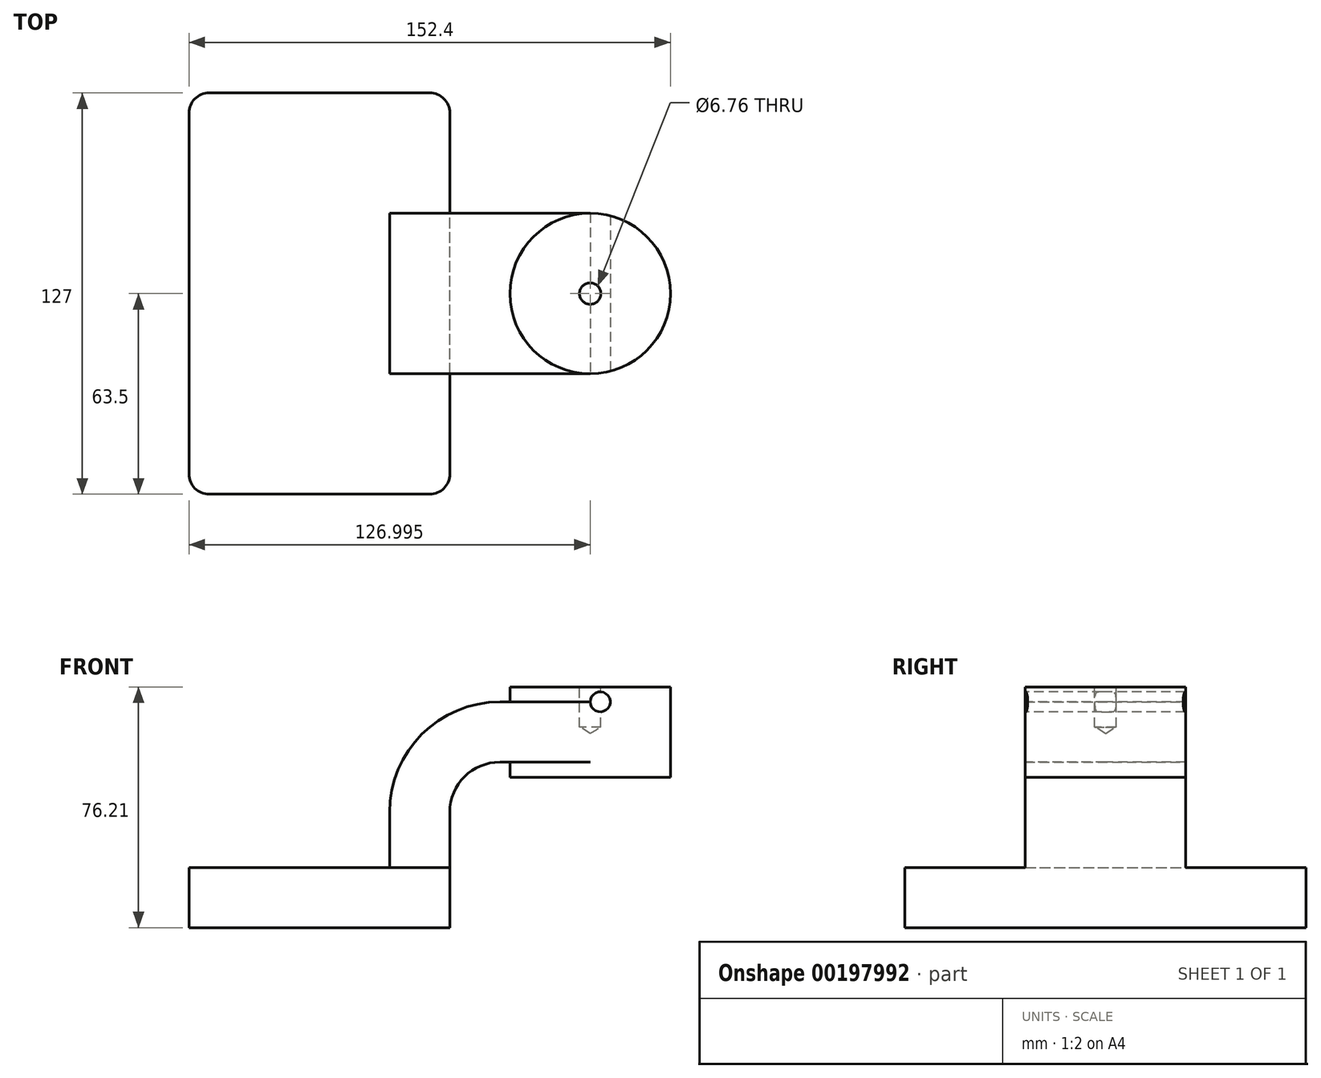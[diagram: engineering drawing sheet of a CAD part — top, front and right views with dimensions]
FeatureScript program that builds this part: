
annotation { "Feature Type Name" : "Feature", "Feature Type Description" : "" }
export const myFeature = defineFeature(function(context is Context, id is Id, definition is map)
    precondition{}
    {
        {
            var Q0;
            Q0=qCreatedBy(makeId("Front.planeOp"),FACE);
            var sketch = newSketch(context, id + "F0", { "sketchPlane" : qUnion([Q0])});
            skLineSegment(sketch, "E0.bottom", {"start": v(41.27, 9.53) * mm, "end": v(-41.27, 9.53) * mm});
            skLineSegment(sketch, "E0.top", {"start": v(41.28, -9.52) * mm, "end": v(-41.27, -9.52) * mm});
            skLineSegment(sketch, "E0.left", {"start": v(41.27, 9.53) * mm, "end": v(41.27, -9.52) * mm});
            skLineSegment(sketch, "E0.right", {"start": v(-41.27, 9.53) * mm, "end": v(-41.27, -9.52) * mm});
            skPoint(sketch, "E0.middle", {"position": v(0, 0) * mm});
            skLineSegment(sketch, "E1.bottom", {"start": v(111.13, 38.1) * mm, "end": v(60.32, 38.1) * mm});
            skLineSegment(sketch, "E1.top", {"start": v(111.13, 66.68) * mm, "end": v(60.32, 66.68) * mm});
            skLineSegment(sketch, "E1.left", {"start": v(111.13, 38.1) * mm, "end": v(111.13, 66.68) * mm});
            skLineSegment(sketch, "E1.right", {"start": v(60.32, 38.1) * mm, "end": v(60.32, 66.68) * mm});
            skPoint(sketch, "E1.middle", {"position": v(85.72, 52.39) * mm});
            skLineSegment(sketch, "E2", {"start": v(41.27, 9.53) * mm, "end": v(41.27, 27) * mm});
            skArc(sketch, "E3", {"start": v(41.27, 27) * mm, "mid": v(45.92, 38.23) * mm, "end": v(57.15, 42.88) * mm});
            skLineSegment(sketch, "E4", {"start": v(57.15, 42.88) * mm, "end": v(85.72, 42.88) * mm});
            skLineSegment(sketch, "E5.0", {"start": v(57.15, 61.93) * mm, "end": v(85.72, 61.93) * mm});
            skArc(sketch, "E5.1", {"start": v(22.22, 27) * mm, "mid": v(32.45, 51.7) * mm, "end": v(57.15, 61.93) * mm});
            skLineSegment(sketch, "E5.2", {"start": v(22.22, 9.53) * mm, "end": v(22.22, 27) * mm});
            skLineSegment(sketch, "E6", {"start": v(85.72, 38.1) * mm, "end": v(85.72, 66.68) * mm});
            skFitSpline(sketch, "E7", {"points": [v(-41.27, 9.52) * mm, v(57.15, 61.93) * mm], "startDerivative": vector(0, 75.97) * mm, "endDerivative": vector(143.41, 0) * mm});
            skSolve(sketch);
        }
        {
            var Q0;
            Q0=makeQuery(id+"F0.imprint","IMPRINT",FACE,{"disambiguationData":[TD([[makeQuery(id+"F0.imprint","IMPRINT",EDGE,{"derivedFrom":sQuery(id+"F0.wireOp",EDGE,"E0.top")}),-1.0]])]});
            extrude(context, id + "F1", {"entities" : qUnion([Q0]), "endBound" : BoundingType.SYMMETRIC, "depth" : 127 * mm});
        }
        {
            var Q0;
            {var subQ1=sQuery(id+"F0.wireOp",EDGE,"E2");Q0=makeQuery(id+"F0.imprint","IMPRINT",FACE,{"disambiguationData":[TD([[makeQuery(id+"F0.imprint","IMPRINT",EDGE,{"derivedFrom":subQ1}),1.0]])]});}
            var Q1;
            {var subQ0=sQuery(id+"F0.wireOp",EDGE,"E4");var subQ1=sQuery(id+"F0.wireOp",EDGE,"E1.right");var subQ2=makeQuery(id+"F0.imprint","INTERSECT",VERTEX,{"derivedFrom":[subQ1,subQ0]});Q1=makeQuery(id+"F0.imprint","IMPRINT",FACE,{"disambiguationData":[TD([[makeQuery(id+"F0.imprint","IMPRINT",EDGE,{"disambiguationData":[TD([[subQ2,-1.0]])],"derivedFrom":subQ1}),-1.0]])]});}
            extrude(context, id + "F2", {"entities" : qUnion([Q0, Q1]), "operationType" : NewBodyOperationType.ADD, "endBound" : BoundingType.SYMMETRIC, "depth" : 50.8 * mm});
        }
        {
            var Q0;
            Q0=makeQuery(id+"F0.imprint","IMPRINT",FACE,{"disambiguationData":[TD([[makeQuery(id+"F0.imprint","IMPRINT",EDGE,{"derivedFrom":sQuery(id+"F0.wireOp",EDGE,"E5.1")}),1.0]])]});
            extrude(context, id + "F3", {"entities" : qUnion([Q0]), "operationType" : NewBodyOperationType.ADD, "endBound" : BoundingType.SYMMETRIC, "depth" : 15.88 * mm});
        }
        {
            var Q0;
            {var subQ0=sQuery(id+"F0.wireOp",EDGE,"E1.left");Q0=makeQuery(id+"F0.imprint","IMPRINT",FACE,{"disambiguationData":[TD([[makeQuery(id+"F0.imprint","IMPRINT",EDGE,{"derivedFrom":subQ0}),1.0]])]});}
            var Q1;
            Q1=sQuery(id+"F0.wireOp",EDGE,"E6");
            revolve(context, id + "F4", {"operationType" : NewBodyOperationType.ADD, "entities" : qUnion([Q0]), "axis" : qUnion([Q1]), "revolveType" : RevolveType.FULL});
        }
        {
            var Q0;
            Q0=makeQuery(id+"F1.opExtrude","CAP_EDGE",EDGE,{"disambiguationData":[OSD([sQuery(id+"F0.wireOp",EDGE,"E0.left")])],"isStart":false});
            var Q1;
            Q1=makeQuery(id+"F1.opExtrude","CAP_EDGE",EDGE,{"disambiguationData":[OSD([sQuery(id+"F0.wireOp",EDGE,"E0.right")])],"isStart":false});
            var Q2;
            Q2=makeQuery(id+"F1.opExtrude","CAP_EDGE",EDGE,{"disambiguationData":[OSD([sQuery(id+"F0.wireOp",EDGE,"E0.left")])],"isStart":true});
            var Q3;
            Q3=makeQuery(id+"F1.opExtrude","CAP_EDGE",EDGE,{"disambiguationData":[OSD([sQuery(id+"F0.wireOp",EDGE,"E0.right")])],"isStart":true});
            fillet(context, id + "F5", {"entities" : qUnion([Q0, Q1, Q2, Q3]), "radius" : 6.35 * mm, "tangentPropagation" : true, "allowEdgeOverflow" : false});
        }
        {
            var Q0;
            Q0=makeQuery(id+"F4.opRevolve","SWEPT_FACE",FACE,{"disambiguationData":[OSD([sQuery(id+"F0.wireOp",EDGE,"E1.top")])]});
            var sketch = newSketch(context, id + "F6", { "sketchPlane" : qUnion([Q0])});
            skPoint(sketch, "E8", {"position": v(85.72, 0) * mm});
            skSolve(sketch);
        }
        {
            var Q0;
            Q0=sQuery(id+"F6.wireOp",VERTEX,"E8");
            var Q1;
            Q1=makeQuery(id+"F1.opExtrude","SWEPT_BODY",BODY,{"disambiguationData":[OSD([sQuery(id+"F0.wireOp",EDGE,"E0.bottom"),sQuery(id+"F0.wireOp",EDGE,"E0.top"),sQuery(id+"F0.wireOp",EDGE,"E0.left"),sQuery(id+"F0.wireOp",EDGE,"E0.right")])]});
            hole(context, id + "F7", {"style" : HoleStyle.SIMPLE, "endStyle" : HoleEndStyle.BLIND, "standardTappedOrClearance" : lookupTablePath({ "standard" : "ANSI", "fit" : "Normal (ASME)", "size" : "1/4", "type" : "Clearance" }), "standardBlindInLast" : lookupTablePath({ "fit" : "Free", "standard" : "ANSI", "size" : "1/4", "type" : "Clearance" }), "holeDiameter" : 6.76 * mm, "holeDepth" : 12.7 * mm, "startFromSketch" : true, "locations" : qUnion([Q0]), "scope" : qUnion([Q1])});
        }
        {
            var Q0;
            Q0=makeQuery(id+"F2.opExtrude","CAP_FACE",FACE,{"disambiguationData":[OSD([sQuery(id+"F0.wireOp",EDGE,"E0.bottom"),sQuery(id+"F0.wireOp",EDGE,"E2"),sQuery(id+"F0.wireOp",EDGE,"E3"),sQuery(id+"F0.wireOp",EDGE,"E4"),sQuery(id+"F0.wireOp",EDGE,"E5.0"),sQuery(id+"F0.wireOp",EDGE,"E5.1"),sQuery(id+"F0.wireOp",EDGE,"E5.2"),sQuery(id+"F0.wireOp",EDGE,"E6")])],"isStart":false});
            var sketch = newSketch(context, id + "F8", { "sketchPlane" : qUnion([Q0])});
            skLineSegment(sketch, "E9", {"start": v(85.72, 61.93) * mm, "end": v(88.9, 61.93) * mm});
            skPoint(sketch, "E10", {"position": v(88.9, 61.93) * mm});
            skSolve(sketch);
        }
        {
            var Q0;
            Q0=sQuery(id+"F8.wireOp",VERTEX,"E10");
            var Q1;
            Q1=makeQuery(id+"F1.opExtrude","SWEPT_BODY",BODY,{"disambiguationData":[OSD([sQuery(id+"F0.wireOp",EDGE,"E0.bottom"),sQuery(id+"F0.wireOp",EDGE,"E0.top"),sQuery(id+"F0.wireOp",EDGE,"E0.left"),sQuery(id+"F0.wireOp",EDGE,"E0.right")])]});
            hole(context, id + "F9", {"style" : HoleStyle.SIMPLE, "endStyle" : HoleEndStyle.THROUGH, "holeDiameter" : 6.35 * mm, "startFromSketch" : true, "locations" : qUnion([Q0]), "scope" : qUnion([Q1]), "isTappedThrough" : true});
        }
    });
